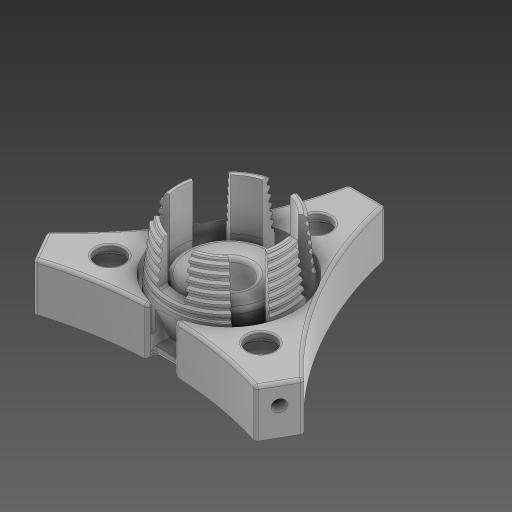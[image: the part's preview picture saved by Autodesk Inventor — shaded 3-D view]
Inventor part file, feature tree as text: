
AUTODESK INVENTOR PART (.ipt)
format: ipt  version: 2024 (Build 280153000, 153)  size: 1,716,736 bytes
history: native  units: mm
features: sketch x17, extrude x12, fillet x9, chamfer x3, hole x3, draft x2, helix x2, plane x2, pattern_circular x2, projected_geometry x2
ambient origin geometry x8: Origin, YZ Plane, XZ Plane, XY Plane, X Axis, Y Axis, Z Axis, Center Point
bodies: Solid1 (feature_tree)
feature tree (54):
  extrude  "Extrusion1"  Depth=29.5mm
  draft  "FaceDraft1"
  sketch  "Sketch2"  dims[d7=6.806784mm d8=0.55605mm]
  helix  "Coil1"  [1 undecoded]
  helix  "Coil2"  [1 undecoded]
  extrude  "Extrusion2"  Depth=0.55605mm
  extrude  "Extrusion3"  TaperAngle=0.0deg  [1 undecoded]
  fillet  "Fillet1"  [1 undecoded]
  chamfer  "Chamfer1"  Distance=0.3mm Angle=45.0deg
  plane  "Work Plane1"
  extrude  "Extrusion4"  TaperAngle=0.0deg  [1 undecoded]
  extrude  "Extrusion8"  Depth=60.0mm TaperAngle=360.0deg
  hole  "Hole2"  [1 undecoded]
  sketch  "Sketch13"  dims[d58=6.0mm d65=60.0mm d67=360.0deg]
  extrude  "Extrusion11"  Depth=10.0mm TaperAngle=0.0deg
  hole  "Bearing Hole"  [1 undecoded]
  pattern_circular  "Circular Pattern4"  Count=3 Angle=360.0deg
  extrude  "Extrusion13"  Depth=7.0mm TaperAngle=0.0deg
  sketch  "Sketch20"  dims[d126=6.804mm d127=6.0mm d128=9.979mm d129=8.89mm d130=90.0deg d131=8.0mm d132=20.594885mm d133=22.0mm d134=30.0mm d135=360.0deg]
  extrude  "Extrusion14"  Depth=1.55mm TaperAngle=45.0deg
  sketch  "Sketch18"  dims[d124=34.0mm]
  fillet  "Fillet9"  Radius=0.24mm
  chamfer  "Chamfer4"  [1 undecoded]
  chamfer  "Chamfer5"  Distance=0.5mm
  fillet  "Fillet11"  Radius=2.0mm
  draft  "FaceDraft2"
  fillet  "Fillet13"  Radius=34.767mm
  extrude  "Extrusion15"  Depth=0.5mm
  hole  "Hole5"  [1 undecoded]
  pattern_circular  "Circular Pattern5"  [2 undecoded]
  plane  "Work Plane4"
  extrude  "Extrusion16"  Depth=0.5mm
  fillet  "Fillet14"  Radius=30.0mm
  fillet  "Fillet16"  Radius=16.0mm
  extrude  "Extrusion17"  TaperAngle=0.0deg  [1 undecoded]
  extrude  "Extrusion19"  Depth=0.5mm
  fillet  "Fillet17"  Radius=0.4mm
  fillet  "Fillet18"  Radius=25.0mm
  fillet  "Fillet19"  Radius=22.0mm
  sketch  "Sketch1"  dims[d0=24.8mm d1=29.5mm d2=12.875mm d3=0.0mm d4=1.047198mm]
  projected_geometry  "Projected Loop1"
  sketch  "Sketch3"  dims[d9=6.806784mm]
  sketch  "Sketch4"  dims[d10=2.0mm d11=10.0mm d12=70.0mm d13=-1.047198mm d14=90.0deg d15=90.0deg d16=0.0mm d17=0.0mm d18=0.6mm]
  sketch  "Sketch5"  dims[d19=2.0mm d20=10.0mm d21=10.0mm d22=1.047198mm d23=90.0deg d24=90.0deg d25=0.0mm d26=0.0mm d27=0.0mm d28=0.0mm d29=0.0mm d30=0.0mm]
  sketch  "Sketch10"  dims[d31=0.6mm d32=0.3mm d33=2.0mm d34=45.0deg]
  sketch  "Sketch11"  dims[d36=-2.0mm d42=0.0mm d43=0.0mm]
  sketch  "Sketch15"  dims[d91=33.0mm d92=12.0mm d93=0.0mm]
  sketch  "Sketch17"  dims[d94=5.3mm d95=6.0mm d96=10.0mm d97=7.0mm d98=90.0deg d99=8.0mm d100=20.594885mm d122=10.0mm d123=0.0mm]
  sketch  "Sketch21"  dims[d146=11.34464mm d147=7.0mm d148=0.0mm]
  sketch  "Sketch22"  dims[d150=1.0mm d151=1.55mm d152=2.0mm d153=45.0deg]
  sketch  "Sketch25"  dims[d154=0.5mm d155=2.0mm d156=45.0deg d158=0.24mm]
  sketch  "Sketch26"  dims[d160=1.25mm d161=0.0mm d162=0.0mm]
  sketch  "Sketch28"  dims[d163=30.0deg d164=0.5mm d165=2.0mm d166=34.767mm d167=9.0mm d168=30.0deg d169=7.0mm d170=0.0mm d171=3.0mm d172=6.0mm d173=9.779mm d174=7.62mm d175=90.0deg d176=7.0mm d177=0.0mm d178=5.0mm d179=30.0mm d180=360.0deg d182=16.0mm d183=0.0mm d184=0.0mm d185=0.75mm d187=0.4mm d188=25.0mm d189=22.0mm d190=31.0mm d191=7.0mm d192=0.0mm d193=32.8mm d208=9.0mm d209=0.0mm d210=1.0mm d211=0.25mm d212=0.5mm d213=7.0mm d214=60.0mm d216=360.0deg]
  projected_geometry  "Project Cut Edges3"
note: 12 required parameter values undecoded (feature->parameter linkage not recoverable at this tier; creation-order binding heuristic only, values carry confidence <= 0.55)
